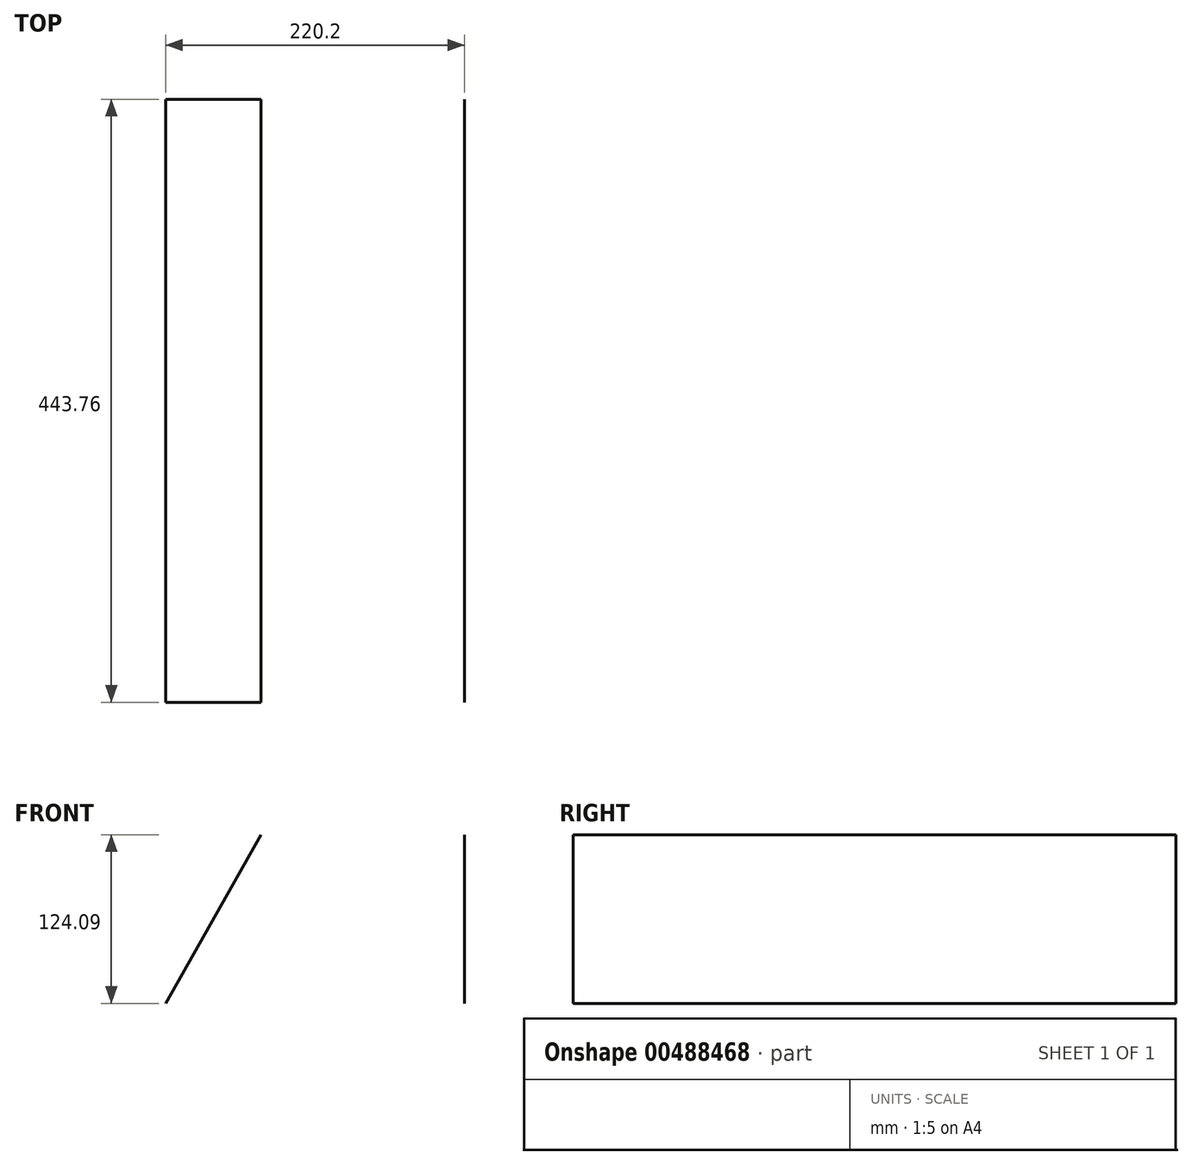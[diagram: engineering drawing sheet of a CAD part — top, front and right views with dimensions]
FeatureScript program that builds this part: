
annotation { "Feature Type Name" : "Feature", "Feature Type Description" : "" }
export const myFeature = defineFeature(function(context is Context, id is Id, definition is map)
    precondition{}
    {
        {
            var Q0;
            Q0=qCreatedBy(makeId("Front.planeOp"),FACE);
            var sketch = newSketch(context, id + "F0", { "sketchPlane" : qUnion([Q0])});
            skLineSegment(sketch, "E0", {"start": v(-107, 0) * mm, "end": v(-36.8, 124.09) * mm});
            skLineSegment(sketch, "E1", {"start": v(113.2, 0) * mm, "end": v(113.2, 124.09) * mm});
            skSolve(sketch);
        }
        {
            var Q0;
            Q0=sQuery(id+"F0.wireOp",EDGE,"E0");
            extrude(context, id + "F1", {"bodyType" : ToolBodyType.SURFACE, "surfaceEntities" : qUnion([Q0]), "endBound" : BoundingType.SYMMETRIC, "depth" : 443.75 * mm});
        }
        {
            var Q0;
            Q0=sQuery(id+"F0.wireOp",EDGE,"E1");
            extrude(context, id + "F2", {"bodyType" : ToolBodyType.SURFACE, "surfaceEntities" : qUnion([Q0]), "endBound" : BoundingType.SYMMETRIC, "depth" : 443.75 * mm});
        }
    });
